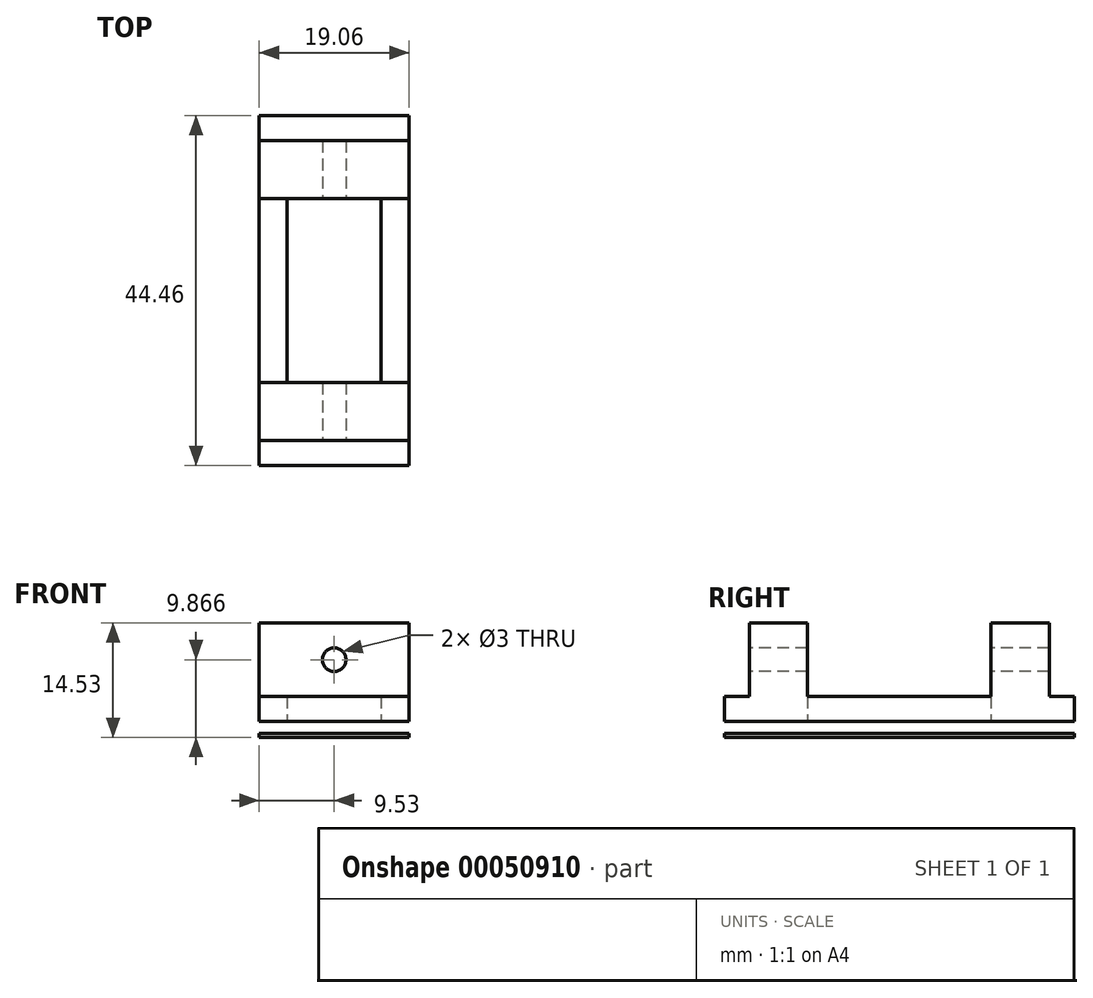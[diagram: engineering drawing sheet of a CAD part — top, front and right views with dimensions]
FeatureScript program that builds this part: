
annotation { "Feature Type Name" : "Feature", "Feature Type Description" : "" }
export const myFeature = defineFeature(function(context is Context, id is Id, definition is map)
    precondition{}
    {
        {
            var Q0;
            Q0=qCreatedBy(makeId("Top.planeOp"),FACE);
            var sketch = newSketch(context, id + "F0", { "sketchPlane" : qUnion([Q0])});
            skLineSegment(sketch, "E0.rect.bottom", {"start": v(-5.97, 11.68) * mm, "end": v(5.97, 11.68) * mm});
            skLineSegment(sketch, "E0.rect.top", {"start": v(-5.97, -11.68) * mm, "end": v(5.97, -11.68) * mm});
            skLineSegment(sketch, "E0.rect.left", {"start": v(-5.97, 11.68) * mm, "end": v(-5.97, -11.68) * mm});
            skLineSegment(sketch, "E0.rect.right", {"start": v(5.97, 11.68) * mm, "end": v(5.97, -11.68) * mm});
            skPoint(sketch, "E0.rect.middle", {"position": v(0, 0) * mm});
            skLineSegment(sketch, "E1.rect.bottom", {"start": v(-9.52, 19.05) * mm, "end": v(9.53, 19.05) * mm});
            skLineSegment(sketch, "E1.rect.top", {"start": v(-9.53, -19.05) * mm, "end": v(9.53, -19.05) * mm});
            skLineSegment(sketch, "E1.rect.left", {"start": v(-9.52, 19.05) * mm, "end": v(-9.53, -19.05) * mm});
            skLineSegment(sketch, "E1.rect.right", {"start": v(9.53, 19.05) * mm, "end": v(9.53, -19.05) * mm});
            skSolve(sketch);
        }
        {
            var Q0;
            Q0 = qSketchRegion(id + "F0", true);
            extrude(context, id + "F1", {"entities" : qUnion([Q0]), "depth" : 12.5 * mm});
        }
        {
            var Q0;
            Q0=makeQuery(id+"F1.opExtrude","CAP_FACE",FACE,{"disambiguationData":[OSD([sQuery(id+"F0.wireOp",EDGE,"E0.rect.bottom"),sQuery(id+"F0.wireOp",EDGE,"E0.rect.top"),sQuery(id+"F0.wireOp",EDGE,"E0.rect.left"),sQuery(id+"F0.wireOp",EDGE,"E0.rect.right"),sQuery(id+"F0.wireOp",EDGE,"E1.rect.bottom"),sQuery(id+"F0.wireOp",EDGE,"E1.rect.top"),sQuery(id+"F0.wireOp",EDGE,"E1.rect.left"),sQuery(id+"F0.wireOp",EDGE,"E1.rect.right")])],"isStart":true});
            var sketch = newSketch(context, id + "F2", { "sketchPlane" : qUnion([Q0])});
            skLineSegment(sketch, "E2.rect.bottom", {"start": v(-9.52, -22.23) * mm, "end": v(9.53, -22.22) * mm});
            skLineSegment(sketch, "E2.rect.top", {"start": v(-9.53, 22.22) * mm, "end": v(9.52, 22.23) * mm});
            skLineSegment(sketch, "E2.rect.left", {"start": v(-9.52, -22.22) * mm, "end": v(-9.53, 22.22) * mm});
            skLineSegment(sketch, "E2.rect.right", {"start": v(9.53, -22.22) * mm, "end": v(9.52, 22.22) * mm});
            skPoint(sketch, "E2.rect.middle", {"position": v(0, 0) * mm});
            skLineSegment(sketch, "E3.bottom", {"start": v(-5.97, -11.68) * mm, "end": v(5.97, -11.68) * mm});
            skLineSegment(sketch, "E3.top", {"start": v(-5.97, 11.68) * mm, "end": v(5.97, 11.68) * mm});
            skLineSegment(sketch, "E3.left", {"start": v(-5.97, -11.68) * mm, "end": v(-5.97, 11.68) * mm});
            skLineSegment(sketch, "E3.right", {"start": v(5.97, -11.68) * mm, "end": v(5.97, 11.68) * mm});
            skSolve(sketch);
        }
        {
            var Q0;
            Q0 = qSketchRegion(id + "F2", true);
            extrude(context, id + "F3", {"entities" : qUnion([Q0]), "operationType" : NewBodyOperationType.ADD, "oppositeDirection" : true, "depth" : 3.17 * mm});
        }
        {
            var Q0;
            Q0=makeQuery(id+"F1.opExtrude","CAP_FACE",FACE,{"disambiguationData":[OSD([sQuery(id+"F0.wireOp",EDGE,"E0.rect.bottom"),sQuery(id+"F0.wireOp",EDGE,"E0.rect.top"),sQuery(id+"F0.wireOp",EDGE,"E0.rect.left"),sQuery(id+"F0.wireOp",EDGE,"E0.rect.right"),sQuery(id+"F0.wireOp",EDGE,"E1.rect.bottom"),sQuery(id+"F0.wireOp",EDGE,"E1.rect.top"),sQuery(id+"F0.wireOp",EDGE,"E1.rect.left"),sQuery(id+"F0.wireOp",EDGE,"E1.rect.right")])],"isStart":false});
            var sketch = newSketch(context, id + "F4", { "sketchPlane" : qUnion([Q0])});
            skLineSegment(sketch, "E4.bottom", {"start": v(-5.97, -11.68) * mm, "end": v(-9.52, -11.68) * mm});
            skLineSegment(sketch, "E4.top", {"start": v(-5.97, 11.68) * mm, "end": v(-9.52, 11.68) * mm});
            skLineSegment(sketch, "E4.left", {"start": v(-5.97, -11.68) * mm, "end": v(-5.97, 11.68) * mm});
            skLineSegment(sketch, "E4.right", {"start": v(-9.52, -11.68) * mm, "end": v(-9.52, 11.68) * mm});
            skLineSegment(sketch, "E5.bottom", {"start": v(5.97, 11.68) * mm, "end": v(9.53, 11.68) * mm});
            skLineSegment(sketch, "E5.top", {"start": v(5.97, -11.68) * mm, "end": v(9.53, -11.68) * mm});
            skLineSegment(sketch, "E5.left", {"start": v(5.97, 11.68) * mm, "end": v(5.97, -11.68) * mm});
            skLineSegment(sketch, "E5.right", {"start": v(9.53, 11.68) * mm, "end": v(9.53, -11.68) * mm});
            skSolve(sketch);
        }
        {
            var Q0;
            Q0 = qSketchRegion(id + "F4", true);
            var Q1;
            {var subQ0=sQuery(id+"F2.wireOp",EDGE,"E2.rect.top");var subQ1=sQuery(id+"F2.wireOp",EDGE,"E2.rect.left");var subQ2=sQuery(id+"F2.wireOp",EDGE,"E2.rect.right");Q1=makeQuery(id+"F3.boolean.opBoolean","SPLIT",FACE,{"disambiguationData":[TD([makeQuery(id+"F1.opExtrude","SWEPT_FACE",FACE,{"disambiguationData":[OSD([sQuery(id+"F0.wireOp",EDGE,"E1.rect.top")])]})])],"derivedFrom":makeQuery(id+"F3.opExtrude","CAP_FACE",FACE,{"disambiguationData":[OSD([sQuery(id+"F2.wireOp",EDGE,"E2.rect.bottom"),subQ0,subQ1,subQ2,sQuery(id+"F2.wireOp",EDGE,"E3.bottom"),sQuery(id+"F2.wireOp",EDGE,"E3.top"),sQuery(id+"F2.wireOp",EDGE,"E3.left"),sQuery(id+"F2.wireOp",EDGE,"E3.right")])],"isStart":false})});}
            extrude(context, id + "F5", {"entities" : qUnion([Q0]), "operationType" : NewBodyOperationType.REMOVE, "endBound" : BoundingType.UP_TO_SURFACE, "oppositeDirection" : true, "endBoundEntityFace" : qUnion([Q1]), "depth" : 25.4 * mm});
        }
        {
            var Q0;
            Q0=makeQuery(id+"F1.opExtrude","SWEPT_FACE",FACE,{"disambiguationData":[OSD([sQuery(id+"F0.wireOp",EDGE,"E1.rect.top")])]});
            var sketch = newSketch(context, id + "F6", { "sketchPlane" : qUnion([Q0])});
            skLineSegment(sketch, "E6", {"start": v(0, 12.5) * mm, "end": v(0, 3.18) * mm, "construction": true});
            skCircle(sketch, "E7", {"center": v(0, 7.84) * mm, "radius": 1.5 * mm});
            skSolve(sketch);
        }
        {
            var Q0;
            Q0 = qSketchRegion(id + "F6", true);
            extrude(context, id + "F7", {"entities" : qUnion([Q0]), "operationType" : NewBodyOperationType.REMOVE, "endBound" : BoundingType.THROUGH_ALL, "oppositeDirection" : true, "depth" : 25.4 * mm});
        }
        {
            var Q0;
            Q0=makeQuery(id+"F3.boolean.opBoolean","MERGE",FACE,{"derivedFrom":[makeQuery(id+"F1.opExtrude","CAP_FACE",FACE,{"disambiguationData":[OSD([sQuery(id+"F0.wireOp",EDGE,"E0.rect.bottom"),sQuery(id+"F0.wireOp",EDGE,"E0.rect.top"),sQuery(id+"F0.wireOp",EDGE,"E0.rect.left"),sQuery(id+"F0.wireOp",EDGE,"E0.rect.right"),sQuery(id+"F0.wireOp",EDGE,"E1.rect.bottom"),sQuery(id+"F0.wireOp",EDGE,"E1.rect.top"),sQuery(id+"F0.wireOp",EDGE,"E1.rect.left"),sQuery(id+"F0.wireOp",EDGE,"E1.rect.right")])],"isStart":true}),makeQuery(id+"F3.opExtrude","CAP_FACE",FACE,{"disambiguationData":[OSD([sQuery(id+"F2.wireOp",EDGE,"E2.rect.bottom"),sQuery(id+"F2.wireOp",EDGE,"E2.rect.top"),sQuery(id+"F2.wireOp",EDGE,"E2.rect.left"),sQuery(id+"F2.wireOp",EDGE,"E2.rect.right"),sQuery(id+"F2.wireOp",EDGE,"E3.bottom"),sQuery(id+"F2.wireOp",EDGE,"E3.top"),sQuery(id+"F2.wireOp",EDGE,"E3.left"),sQuery(id+"F2.wireOp",EDGE,"E3.right")])],"isStart":true})]});
            cPlane(context, id + "F8", {"entities" : qUnion([Q0]), "cplaneType" : CPlaneType.OFFSET, "offset" : 1.52 * mm, "width" : 152.4 * mm, "height" : 152.4 * mm});
        }
        {
            var Q0;
            Q0=qCreatedBy(id+"F8.planeOp",FACE);
            var sketch = newSketch(context, id + "F9", { "sketchPlane" : qUnion([Q0])});
            skLineSegment(sketch, "E8.bottom", {"start": v(9.53, -22.22) * mm, "end": v(-9.52, -22.22) * mm});
            skLineSegment(sketch, "E8.top", {"start": v(9.52, 22.23) * mm, "end": v(-9.53, 22.22) * mm});
            skLineSegment(sketch, "E8.left", {"start": v(9.53, -22.22) * mm, "end": v(9.52, 22.22) * mm});
            skLineSegment(sketch, "E8.right", {"start": v(-9.52, -22.22) * mm, "end": v(-9.53, 22.22) * mm});
            skSolve(sketch);
        }
        {
            var Q0;
            Q0 = qSketchRegion(id + "F9", true);
            extrude(context, id + "F10", {"entities" : qUnion([Q0]), "depth" : 0.5 * mm});
        }
    });
